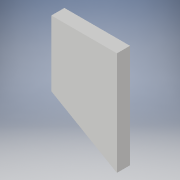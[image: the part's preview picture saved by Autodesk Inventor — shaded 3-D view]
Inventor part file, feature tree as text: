
AUTODESK INVENTOR PART (.ipt)
format: ipt  version: 2017 (Build 210142000, 142)  size: 258,560 bytes
history: native  units: in
note: dims shown in document units (in); Inventor stores cm internally (conversion verified against a paired STEP export)
features: extrude x3, sketch x1
ambient origin geometry x8: Origin, YZ Plane, XZ Plane, XY Plane, X Axis, Y Axis, Z Axis, Center Point
bodies: Solid1 (feature_tree)
feature tree (4):
  extrude  "door"  Depth=5.0in TaperAngle=0.0deg
  sketch  "Sketch3"  dims[d143=10.0in d144=0.0in d439=5.0in d440=0.0in d441=5.0in d442=0.0in d448=78.8675in]
  extrude  "connection give"  Depth=5.0in TaperAngle=0.0deg
  extrude  "connection receive"  Depth=5.0in
